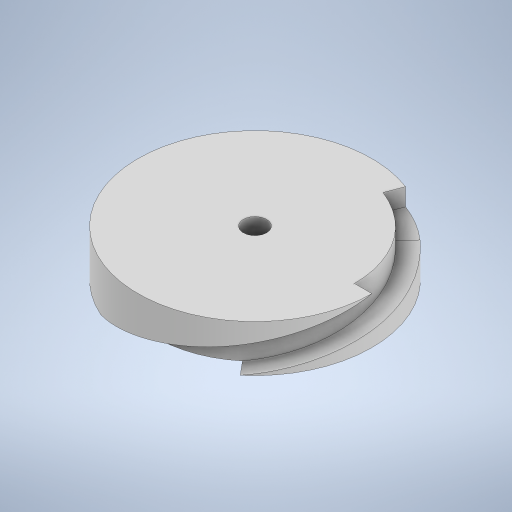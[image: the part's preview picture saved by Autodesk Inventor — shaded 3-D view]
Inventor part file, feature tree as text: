
AUTODESK INVENTOR PART (.ipt)
format: ipt  version: 2023 (Build 270158000, 158)  size: 269,312 bytes
history: native  units: in
note: dims shown in document units (in); Inventor stores cm internally (conversion verified against a paired STEP export)
features: sketch x4, extrude x3, plane x1, emboss x1
ambient origin geometry x8: Origin, YZ Plane, XZ Plane, XY Plane, X Axis, Y Axis, Z Axis, Center Point
bodies: Solid1 (feature_tree)
feature tree (9):
  extrude  "Extrusion1"  Depth=0.4in TaperAngle=0.0deg
  plane  "Work Plane1"
  emboss  "Emboss1"
  extrude  "Extrusion3"  Depth=1.0in
  extrude  "Extrusion4"  Depth=0.15in TaperAngle=0.0deg
  sketch  "Sketch1"  dims[d0=2.0in d1=0.4in d2=0.0in]
  sketch  "Sketch3"  dims[d6=1.0in d7=0.025in]
  sketch  "Sketch4"  dims[d8=0.15in d9=0.0in d10=0.15in d11=0.0in]
  sketch  "Sketch5"  dims[d12=0.2in d13=1.7875in d14=0.0in]
